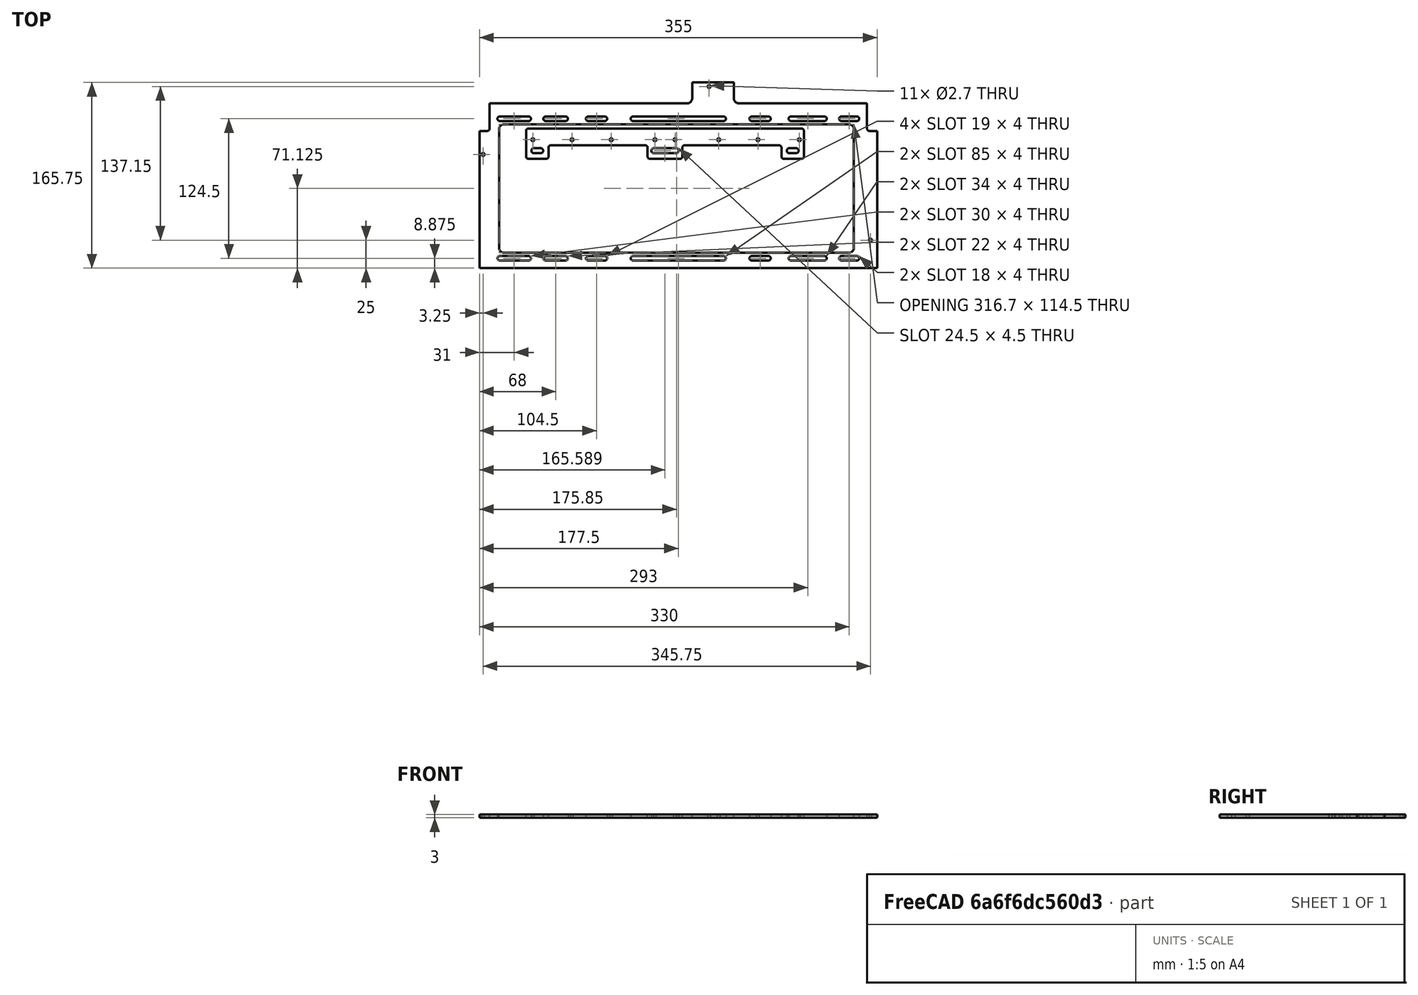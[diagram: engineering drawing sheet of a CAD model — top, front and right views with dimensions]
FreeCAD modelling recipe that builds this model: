
FCSTD DOCUMENT  (FreeCAD 0.19R24291 (Git))
Label: Mesh_Rad_Mount_04
License: All rights reserved
LicenseURL: http://en.wikipedia.org/wiki/All_rights_reserved
objects: Sketcher::SketchObject×2, PartDesign::Pad×2, PartDesign::Body×2, Mesh::Feature×1
note: 8 computed .brp shape members not serialized (recipe doc carries the construction recipe); baked Part::Feature solids carry a one-line shape summary decoded from their .brp

FEATURE [Sketcher::SketchObject] Sketch
  FullyConstrained = true
  MapMode = 5
  Support = -> [XY_Plane]
  expr: Constraints[122] = (142.25mm - 114.5mm) / 2
  expr: Constraints[121] = (124.5mm - 114.5mm) / 2
  sketch-geometry (84):
    g0: LineSegment StartX=190 StartY=152 StartZ=0 EndX=190 EndY=165.75 EndZ=0
    g1: LineSegment StartX=190 StartY=165.75 StartZ=0 EndX=227 EndY=165.75 EndZ=0
    g2: LineSegment StartX=227 StartY=165.75 StartZ=0 EndX=227 EndY=152 EndZ=0
    g3: LineSegment StartX=232 StartY=147 StartZ=0 EndX=346 EndY=147 EndZ=0
    g4: LineSegment StartX=355 StartY=0 StartZ=0 EndX=0 EndY=0 EndZ=0
    g5: LineSegment StartX=7 StartY=122.5 StartZ=0 EndX=0 EndY=122.5 EndZ=0
    g6: LineSegment StartX=0 StartY=0 StartZ=0 EndX=0 EndY=122.5 EndZ=0
    g7: ArcOfCircle CenterX=7 CenterY=124.5 CenterZ=0 NormalX=0 NormalY=0 NormalZ=1 AngleXU=0 Radius=2 StartAngle=4.71239 EndAngle=6.28319
    g8: ArcOfCircle CenterX=18 CenterY=8.875 CenterZ=0 NormalX=0 NormalY=0 NormalZ=1 AngleXU=0 Radius=2 StartAngle=1.5708 EndAngle=4.71239
    g9: ArcOfCircle CenterX=44 CenterY=8.875 CenterZ=0 NormalX=0 NormalY=0 NormalZ=1 AngleXU=0 Radius=2 StartAngle=4.71239 EndAngle=7.85398
    g10: LineSegment StartX=18 StartY=6.875 StartZ=0 EndX=44 EndY=6.875 EndZ=0
    g11: LineSegment StartX=18 StartY=10.875 StartZ=0 EndX=44 EndY=10.875 EndZ=0
    g12: LineSegment StartX=21.7 StartY=128.375 StartZ=0 EndX=330 EndY=128.375 EndZ=0
    g13: LineSegment StartX=334.2 StartY=124.175 StartZ=0 EndX=334.2 EndY=18.075 EndZ=0
    g14: LineSegment StartX=330 StartY=13.875 StartZ=0 EndX=21.7 EndY=13.875 EndZ=0
    g15: LineSegment StartX=17.5 StartY=18.075 StartZ=0 EndX=17.5 EndY=124.175 EndZ=0
    g16: ArcOfCircle CenterX=21.7 CenterY=124.175 CenterZ=0 NormalX=0 NormalY=0 NormalZ=1 AngleXU=0 Radius=4.2 StartAngle=1.5708 EndAngle=3.14159
    g17: ArcOfCircle CenterX=21.7 CenterY=18.075 CenterZ=0 NormalX=0 NormalY=0 NormalZ=1 AngleXU=0 Radius=4.2 StartAngle=3.14159 EndAngle=4.71239
    g18: ArcOfCircle CenterX=330 CenterY=18.075 CenterZ=0 NormalX=0 NormalY=0 NormalZ=1 AngleXU=0 Radius=4.2 StartAngle=4.71239 EndAngle=6.28319
    g19: ArcOfCircle CenterX=330 CenterY=124.175 CenterZ=0 NormalX=0 NormalY=0 NormalZ=1 AngleXU=0 Radius=4.2 StartAngle=1.2e-15 EndAngle=1.5708
    g20: ArcOfCircle CenterX=18 CenterY=133.375 CenterZ=0 NormalX=0 NormalY=0 NormalZ=1 AngleXU=0 Radius=2 StartAngle=1.5708 EndAngle=4.71239
    g21: ArcOfCircle CenterX=44 CenterY=133.375 CenterZ=0 NormalX=0 NormalY=0 NormalZ=1 AngleXU=0 Radius=2 StartAngle=4.71239 EndAngle=7.85398
    g22: LineSegment StartX=18 StartY=131.375 StartZ=0 EndX=44 EndY=131.375 EndZ=0
    g23: LineSegment StartX=18 StartY=135.375 StartZ=0 EndX=44 EndY=135.375 EndZ=0
    g24: ArcOfCircle CenterX=59 CenterY=133.375 CenterZ=0 NormalX=0 NormalY=0 NormalZ=1 AngleXU=0 Radius=2 StartAngle=1.5708 EndAngle=4.71239
    g25: ArcOfCircle CenterX=77 CenterY=133.375 CenterZ=0 NormalX=0 NormalY=0 NormalZ=1 AngleXU=0 Radius=2 StartAngle=4.71239 EndAngle=7.85398
    g26: LineSegment StartX=59 StartY=131.375 StartZ=0 EndX=77 EndY=131.375 EndZ=0
    g27: LineSegment StartX=59 StartY=135.375 StartZ=0 EndX=77 EndY=135.375 EndZ=0
    g28: ArcOfCircle CenterX=278 CenterY=133.375 CenterZ=0 NormalX=0 NormalY=0 NormalZ=1 AngleXU=0 Radius=2 StartAngle=1.5708 EndAngle=4.71239
    g29: ArcOfCircle CenterX=308 CenterY=133.375 CenterZ=0 NormalX=0 NormalY=0 NormalZ=1 AngleXU=0 Radius=2 StartAngle=4.71239 EndAngle=7.85398
    g30: LineSegment StartX=278 StartY=131.375 StartZ=0 EndX=308 EndY=131.375 EndZ=0
    g31: LineSegment StartX=278 StartY=135.375 StartZ=0 EndX=308 EndY=135.375 EndZ=0
    g32: ArcOfCircle CenterX=323 CenterY=133.375 CenterZ=0 NormalX=0 NormalY=0 NormalZ=1 AngleXU=0 Radius=2 StartAngle=1.5708 EndAngle=4.71239
    g33: ArcOfCircle CenterX=337 CenterY=133.375 CenterZ=0 NormalX=0 NormalY=0 NormalZ=1 AngleXU=0 Radius=2 StartAngle=4.71239 EndAngle=7.85398
    g34: LineSegment StartX=323 StartY=131.375 StartZ=0 EndX=337 EndY=131.375 EndZ=0
    g35: LineSegment StartX=323 StartY=135.375 StartZ=0 EndX=337 EndY=135.375 EndZ=0
    g36: ArcOfCircle CenterX=137 CenterY=133.375 CenterZ=0 NormalX=0 NormalY=0 NormalZ=1 AngleXU=0 Radius=2 StartAngle=1.5708 EndAngle=4.71239
    g37: ArcOfCircle CenterX=218 CenterY=133.375 CenterZ=0 NormalX=0 NormalY=0 NormalZ=1 AngleXU=0 Radius=2 StartAngle=4.71239 EndAngle=7.85398
    g38: LineSegment StartX=137 StartY=131.375 StartZ=0 EndX=218 EndY=131.375 EndZ=0
    g39: LineSegment StartX=137 StartY=135.375 StartZ=0 EndX=218 EndY=135.375 EndZ=0
    g40: ArcOfCircle CenterX=59 CenterY=8.875 CenterZ=0 NormalX=0 NormalY=0 NormalZ=1 AngleXU=0 Radius=2 StartAngle=1.5708 EndAngle=4.71239
    g41: ArcOfCircle CenterX=77 CenterY=8.875 CenterZ=0 NormalX=0 NormalY=0 NormalZ=1 AngleXU=0 Radius=2 StartAngle=4.71239 EndAngle=7.85398
    g42: LineSegment StartX=59 StartY=6.875 StartZ=0 EndX=77 EndY=6.875 EndZ=0
    g43: LineSegment StartX=59 StartY=10.875 StartZ=0 EndX=77 EndY=10.875 EndZ=0
    g44: ArcOfCircle CenterX=137 CenterY=8.875 CenterZ=0 NormalX=0 NormalY=0 NormalZ=1 AngleXU=0 Radius=2 StartAngle=1.5708 EndAngle=4.71239
    g45: ArcOfCircle CenterX=218 CenterY=8.875 CenterZ=0 NormalX=0 NormalY=0 NormalZ=1 AngleXU=0 Radius=2 StartAngle=4.71239 EndAngle=7.85398
    g46: LineSegment StartX=137 StartY=6.875 StartZ=0 EndX=218 EndY=6.875 EndZ=0
    g47: LineSegment StartX=137 StartY=10.875 StartZ=0 EndX=218 EndY=10.875 EndZ=0
    g48: ArcOfCircle CenterX=278 CenterY=8.875 CenterZ=0 NormalX=0 NormalY=0 NormalZ=1 AngleXU=0 Radius=2 StartAngle=1.5708 EndAngle=4.71239
    g49: ArcOfCircle CenterX=308 CenterY=8.875 CenterZ=0 NormalX=0 NormalY=0 NormalZ=1 AngleXU=0 Radius=2 StartAngle=4.71239 EndAngle=7.85398
    g50: LineSegment StartX=278 StartY=6.875 StartZ=0 EndX=308 EndY=6.875 EndZ=0
    g51: LineSegment StartX=278 StartY=10.875 StartZ=0 EndX=308 EndY=10.875 EndZ=0
    g52: ArcOfCircle CenterX=323 CenterY=8.875 CenterZ=0 NormalX=0 NormalY=0 NormalZ=1 AngleXU=0 Radius=2 StartAngle=1.5708 EndAngle=4.71239
    g53: ArcOfCircle CenterX=337 CenterY=8.875 CenterZ=0 NormalX=0 NormalY=0 NormalZ=1 AngleXU=0 Radius=2 StartAngle=4.71239 EndAngle=7.85398
    g54: LineSegment StartX=323 StartY=6.875 StartZ=0 EndX=337 EndY=6.875 EndZ=0
    g55: LineSegment StartX=323 StartY=10.875 StartZ=0 EndX=337 EndY=10.875 EndZ=0
    g56: Circle CenterX=3.25 CenterY=101.5 CenterZ=0 NormalX=0 NormalY=0 NormalZ=1 AngleXU=0 Radius=1.35
    g57: Circle CenterX=205 CenterY=162.15 CenterZ=0 NormalX=0 NormalY=0 NormalZ=1 AngleXU=0 Radius=1.35
    g58: Circle CenterX=349 CenterY=25 CenterZ=0 NormalX=0 NormalY=0 NormalZ=1 AngleXU=0 Radius=1.35
    g59: LineSegment StartX=346 StartY=147 StartZ=0 EndX=346 EndY=124.5 EndZ=0
    g60: LineSegment StartX=348 StartY=122.5 StartZ=0 EndX=355 EndY=122.5 EndZ=0
    g61: LineSegment StartX=355 StartY=0 StartZ=0 EndX=355 EndY=122.5 EndZ=0
    g62: ArcOfCircle CenterX=348 CenterY=124.5 CenterZ=0 NormalX=0 NormalY=0 NormalZ=1 AngleXU=0 Radius=2 StartAngle=3.14159 EndAngle=4.71239
    g63: ArcOfCircle CenterX=232 CenterY=152 CenterZ=0 NormalX=0 NormalY=0 NormalZ=1 AngleXU=0 Radius=5 StartAngle=3.14159 EndAngle=4.71239
    g64: ArcOfCircle CenterX=185 CenterY=152 CenterZ=0 NormalX=0 NormalY=0 NormalZ=1 AngleXU=0 Radius=5 StartAngle=4.71239 EndAngle=6.28319
    g65: ArcOfCircle CenterX=97 CenterY=133.375 CenterZ=0 NormalX=0 NormalY=0 NormalZ=1 AngleXU=0 Radius=2 StartAngle=1.5708 EndAngle=4.71239
    g66: ArcOfCircle CenterX=112 CenterY=133.375 CenterZ=0 NormalX=0 NormalY=0 NormalZ=1 AngleXU=0 Radius=2 StartAngle=4.71239 EndAngle=7.85398
    g67: LineSegment StartX=97 StartY=131.375 StartZ=0 EndX=112 EndY=131.375 EndZ=0
    g68: LineSegment StartX=97 StartY=135.375 StartZ=0 EndX=112 EndY=135.375 EndZ=0
    g69: ArcOfCircle CenterX=97 CenterY=8.875 CenterZ=0 NormalX=0 NormalY=0 NormalZ=1 AngleXU=0 Radius=2 StartAngle=1.5708 EndAngle=4.71239
    g70: ArcOfCircle CenterX=112 CenterY=8.875 CenterZ=0 NormalX=0 NormalY=0 NormalZ=1 AngleXU=0 Radius=2 StartAngle=4.71239 EndAngle=7.85398
    g71: LineSegment StartX=97 StartY=6.875 StartZ=0 EndX=112 EndY=6.875 EndZ=0
    g72: LineSegment StartX=97 StartY=10.875 StartZ=0 EndX=112 EndY=10.875 EndZ=0
    g73: ArcOfCircle CenterX=243 CenterY=8.875 CenterZ=0 NormalX=0 NormalY=0 NormalZ=1 AngleXU=0 Radius=2 StartAngle=1.5708 EndAngle=4.71239
    g74: ArcOfCircle CenterX=258 CenterY=8.875 CenterZ=0 NormalX=0 NormalY=0 NormalZ=1 AngleXU=0 Radius=2 StartAngle=4.71239 EndAngle=7.85398
    g75: LineSegment StartX=243 StartY=6.875 StartZ=0 EndX=258 EndY=6.875 EndZ=0
    g76: LineSegment StartX=243 StartY=10.875 StartZ=0 EndX=258 EndY=10.875 EndZ=0
    g77: ArcOfCircle CenterX=243 CenterY=133.375 CenterZ=0 NormalX=0 NormalY=0 NormalZ=1 AngleXU=0 Radius=2 StartAngle=1.5708 EndAngle=4.71239
    g78: ArcOfCircle CenterX=258 CenterY=133.375 CenterZ=0 NormalX=0 NormalY=0 NormalZ=1 AngleXU=0 Radius=2 StartAngle=4.71239 EndAngle=7.85398
    g79: LineSegment StartX=243 StartY=131.375 StartZ=0 EndX=258 EndY=131.375 EndZ=0
    g80: LineSegment StartX=243 StartY=135.375 StartZ=0 EndX=258 EndY=135.375 EndZ=0
    g81: LineSegment StartX=185 StartY=147 StartZ=0 EndX=9 EndY=147 EndZ=0
    g82: LineSegment StartX=9 StartY=128 StartZ=0 EndX=9 EndY=147 EndZ=0
    g83: LineSegment StartX=9 StartY=124.5 StartZ=0 EndX=9 EndY=128 EndZ=0
  constraints (217):
    c: Coincident(g0,g1)
    c: Horizontal(g1)
    c: Coincident(g1,g2)
    c: Horizontal(g3)
    c: Horizontal(g4)
    c: Vertical(g2)
    c: Vertical(g0)
    c: Horizontal(g5)
    c: DistanceY(g4,g3) = 147
    c: Coincident(g6,g4)
    c: Coincident(g6,g5)
    c: Tangent(g5,g7) = 1.5708
    c: DistanceX(g4,g4) = 355
    c: Coincident(g4,g-1)
    c: Tangent(g8,g11) = 1.5708
    c: Tangent(g8,g10) = -1.5708
    c: Tangent(g10,g9) = -1.5708
    c: Tangent(g11,g9) = 1.5708
    c: Horizontal(g10)
    c: Equal(g8,g9)
    c: Horizontal(g12)
    c: Horizontal(g14)
    c: Vertical(g13)
    c: Vertical(g15)
    c: Tangent(g12,g16) = 1.5708
    c: Tangent(g15,g16) = 1.5708
    c: Tangent(g15,g17) = 1.5708
    c: Tangent(g14,g17) = 1.5708
    c: Tangent(g14,g18) = 1.5708
    c: Tangent(g13,g18) = 1.5708
    c: Tangent(g12,g19) = 1.5708
    c: Tangent(g13,g19) = 1.5708
    c: Radius(g16) = 4.2
    c: Equal(g16,g17)
    c: Equal(g16,g19)
    c: Equal(g16,g18)
    c: DistanceX(g4,g15) = 17.5
    c: Tangent(g20,g23) = 1.5708
    c: Tangent(g20,g22) = -1.5708
    c: Tangent(g22,g21) = -1.5708
    c: Tangent(g23,g21) = 1.5708
    c: Horizontal(g22)
    c: Equal(g20,g21)
    c: Tangent(g24,g27) = 1.5708
    c: Tangent(g24,g26) = -1.5708
    c: Tangent(g26,g25) = -1.5708
    c: Tangent(g27,g25) = 1.5708
    c: Horizontal(g26)
    c: Equal(g24,g25)
    c: Tangent(g28,g31) = 1.5708
    c: Tangent(g28,g30) = -1.5708
    c: Tangent(g30,g29) = -1.5708
    c: Tangent(g31,g29) = 1.5708
    c: Horizontal(g30)
    c: Equal(g28,g29)
    c: Tangent(g32,g35) = 1.5708
    c: Tangent(g32,g34) = -1.5708
    c: Tangent(g34,g33) = -1.5708
    c: Tangent(g35,g33) = 1.5708
    c: Horizontal(g34)
    c: Equal(g32,g33)
    c: Tangent(g36,g39) = 1.5708
    c: Tangent(g36,g38) = -1.5708
    c: Tangent(g38,g37) = -1.5708
    c: Tangent(g39,g37) = 1.5708
    c: Horizontal(g38)
    c: Equal(g36,g37)
    c: Tangent(g40,g43) = 1.5708
    c: Tangent(g40,g42) = -1.5708
    c: Tangent(g42,g41) = -1.5708
    c: Tangent(g43,g41) = 1.5708
    c: Horizontal(g42)
    c: Equal(g40,g41)
    c: Tangent(g44,g47) = 1.5708
    c: Tangent(g44,g46) = -1.5708
    c: Tangent(g46,g45) = -1.5708
    c: Tangent(g47,g45) = 1.5708
    c: Horizontal(g46)
    c: Equal(g44,g45)
    c: Tangent(g48,g51) = 1.5708
    c: Tangent(g48,g50) = -1.5708
    c: Tangent(g50,g49) = -1.5708
    c: Tangent(g51,g49) = 1.5708
    c: Horizontal(g50)
    c: Equal(g48,g49)
    c: Tangent(g52,g55) = 1.5708
    c: Tangent(g52,g54) = -1.5708
    c: Tangent(g54,g53) = -1.5708
    c: Tangent(g55,g53) = 1.5708
    c: Horizontal(g54)
    c: Equal(g52,g53)
    c: Radius(g52) = 2
    c: Equal(g52,g48)
    c: Equal(g52,g44)
    c: Equal(g52,g40)
    c: Equal(g52,g8)
    c: Equal(g52,g20)
    c: Equal(g52,g24)
    c: Equal(g52,g36)
    c: Equal(g52,g28)
    c: Equal(g52,g32)
    c: Horizontal(g53,g49)
    c: Horizontal(g49,g45)
    c: Horizontal(g45,g41)
    c: Horizontal(g41,g9)
    c: Horizontal(g33,g29)
    c: Horizontal(g29,g25)
    c: Horizontal(g25,g21)
    c: Horizontal(g21,g37)
    c: Vertical(g20,g8)
    c: Vertical(g21,g9)
    c: Vertical(g24,g40)
    c: Vertical(g25,g41)
    c: Vertical(g36,g44)
    c: Vertical(g45,g37)
    c: Vertical(g48,g28)
    c: Vertical(g49,g29)
    c: Vertical(g52,g32)
    c: Vertical(g33,g53)
    c: DistanceY(g8,g20) = 124.5
    c: DistanceY(g14,g12) = 114.5
    c: DistanceY(g8,g14) = 5
    c: DistanceY(g4,g14) = 13.875
    c: DistanceX(g24,g25) = 18
    c: DistanceX(g20,g21) = 26
    c: DistanceX(g21,g24) = 15
    c: DistanceX(g4,g20) = 18
    c: DistanceX(g4,g56) = 3.25
    c: DistanceY(g3,g57) = 15.15
    c: DistanceY(g4,g58) = 25
    c: DistanceX(g58,g4) = 6
    c: Vertical(g59)
    c: Horizontal(g60)
    c: Coincident(g61,g4)
    c: Coincident(g61,g60)
    c: Vertical(g61)
    c: Horizontal(g5,g60)
    c: Tangent(g59,g62) = -1.5708
    c: Tangent(g60,g62) = -1.5708
    c: Radius(g62) = 2
    c: Tangent(g2,g63) = -1.5708
    c: Tangent(g3,g63) = -1.5708
    c: DistanceY(g3,g1) = 18.75
    c: Tangent(g0,g64) = -1.5708
    c: DistanceX(g0,g1) = 37
    c: Radius(g64) = 5
    c: Equal(g64,g63)
    c: DistanceX(g32,g33) = 14
    c: DistanceX(g29,g32) = 15
    c: DistanceX(g28,g29) = 30
    c: DistanceX(g25,g36) = 60
    c: DistanceX(g37,g28) = 60
    c: Diameter(g56) = 2.7
    c: Equal(g56,g57)
    c: Equal(g56,g58)
    c: Tangent(g65,g68) = 1.5708
    c: Tangent(g65,g67) = -1.5708
    c: Tangent(g67,g66) = -1.5708
    c: Tangent(g68,g66) = 1.5708
    c: Horizontal(g67)
    c: Equal(g65,g66)
    c: Tangent(g69,g72) = 1.5708
    c: Tangent(g69,g71) = -1.5708
    c: Tangent(g71,g70) = -1.5708
    c: Tangent(g72,g70) = 1.5708
    c: Horizontal(g71)
    c: Equal(g69,g70)
    c: Tangent(g73,g76) = 1.5708
    c: Tangent(g73,g75) = -1.5708
    c: Tangent(g75,g74) = -1.5708
    c: Tangent(g76,g74) = 1.5708
    c: Horizontal(g75)
    c: Equal(g73,g74)
    c: Tangent(g77,g80) = 1.5708
    c: Tangent(g77,g79) = -1.5708
    c: Tangent(g79,g78) = -1.5708
    c: Tangent(g80,g78) = 1.5708
    c: Horizontal(g79)
    c: Equal(g77,g78)
    c: DistanceX(g25,g65) = 20
    c: DistanceX(g66,g36) = 25
    c: DistanceX(g78,g28) = 20
    c: DistanceX(g37,g77) = 25
    c: Horizontal(g77,g66)
    c: Horizontal(g66,g36)
    c: Diameter(g65) = 4
    c: Equal(g65,g77)
    c: Equal(g65,g73)
    c: Equal(g65,g70)
    c: Horizontal(g70,g44)
    c: Horizontal(g44,g73)
    c: Vertical(g65,g69)
    c: Vertical(g70,g66)
    c: Vertical(g73,g77)
    c: Vertical(g74,g78)
    c: DistanceY(g5,g82) = 5.5
    c: Coincident(g81,g64)
    c: Horizontal(g81)
    c: DistanceY(g82,g81) = 19
    c: DistanceY(g56,g81) = 45.5
    c: Coincident(g82,g81)
    c: Vertical(g82)
    c: Radius(g7) = 2
    c: Coincident(g83,g7)
    c: Coincident(g83,g82)
    c: Vertical(g83)
    c: Vertical(g5,g4)
    c: Horizontal(g64,g3)
    c: DistanceX(g5,g5) = 7
    c: DistanceX(g33,g60) = 18
    c: DistanceX(g57,g60) = 150
    c: DistanceX(g1,g60) = 128
    c: DistanceX(g60,g60) = 7
    c: Coincident(g3,g59)
    c: DistanceX(g19,g33) = 7
    c: Horizontal(g7,g7)
    c: Vertical(g64,g64)
FEATURE [Mesh::Feature] TOP_02__1_  label="TOP_02 (1)"
  Placement = pos=(320,-224.75,0) rot=(0,0,1;0rad)
FEATURE [Sketcher::SketchObject] Sketch001
  FullyConstrained = false
  MapMode = 5
  Support = -> [XY_Plane001]
  expr: Constraints[80] = (31mm - 20mm) / 2
  expr: Constraints[56] = (248mm - 31mm) / 2
  sketch-geometry (44):
    g0: LineSegment StartX=59.5885 StartY=97.6384 StartZ=0 EndX=43.5885 EndY=97.6384 EndZ=0
    g1: LineSegment StartX=41.5885 StartY=99.6384 StartZ=0 EndX=41.5885 EndY=122.638 EndZ=0
    g2: LineSegment StartX=43.5885 StartY=124.638 StartZ=0 EndX=287.588 EndY=124.638 EndZ=0
    g3: LineSegment StartX=289.588 StartY=122.638 StartZ=0 EndX=289.588 EndY=99.6384 EndZ=0
    g4: LineSegment StartX=287.588 StartY=97.6384 StartZ=0 EndX=271.588 EndY=97.6384 EndZ=0
    g5: LineSegment StartX=269.588 StartY=99.6384 StartZ=0 EndX=269.588 EndY=107.638 EndZ=0
    g6: LineSegment StartX=267.588 StartY=109.638 StartZ=0 EndX=183.088 EndY=109.638 EndZ=0
    g7: LineSegment StartX=181.088 StartY=107.638 StartZ=0 EndX=181.088 EndY=99.6384 EndZ=0
    g8: LineSegment StartX=179.088 StartY=97.6384 StartZ=0 EndX=152.088 EndY=97.6384 EndZ=0
    g9: LineSegment StartX=150.088 StartY=99.6384 StartZ=0 EndX=150.088 EndY=107.638 EndZ=0
    g10: LineSegment StartX=148.088 StartY=109.638 StartZ=0 EndX=63.5885 EndY=109.638 EndZ=0
    g11: LineSegment StartX=61.5885 StartY=107.638 StartZ=0 EndX=61.5885 EndY=99.6384 EndZ=0
    g12: ArcOfCircle CenterX=267.588 CenterY=107.638 CenterZ=0 NormalX=0 NormalY=0 NormalZ=1 AngleXU=0 Radius=2 StartAngle=2.1e-15 EndAngle=1.5708
    g13: ArcOfCircle CenterX=63.5885 CenterY=107.638 CenterZ=0 NormalX=0 NormalY=0 NormalZ=1 AngleXU=0 Radius=2 StartAngle=1.5708 EndAngle=3.14159
    g14: ArcOfCircle CenterX=148.088 CenterY=107.638 CenterZ=0 NormalX=0 NormalY=0 NormalZ=1 AngleXU=0 Radius=2 StartAngle=3e-16 EndAngle=1.5708
    g15: ArcOfCircle CenterX=152.088 CenterY=99.6384 CenterZ=0 NormalX=0 NormalY=0 NormalZ=1 AngleXU=0 Radius=2 StartAngle=3.14159 EndAngle=4.71239
    g16: ArcOfCircle CenterX=179.088 CenterY=99.6384 CenterZ=0 NormalX=0 NormalY=0 NormalZ=1 AngleXU=0 Radius=2 StartAngle=4.71239 EndAngle=6.28319
    g17: ArcOfCircle CenterX=271.588 CenterY=99.6384 CenterZ=0 NormalX=0 NormalY=0 NormalZ=1 AngleXU=0 Radius=2 StartAngle=3.14159 EndAngle=4.71239
    g18: ArcOfCircle CenterX=59.5885 CenterY=99.6384 CenterZ=0 NormalX=0 NormalY=0 NormalZ=1 AngleXU=0 Radius=2 StartAngle=4.71239 EndAngle=6.28319
    g19: ArcOfCircle CenterX=43.5885 CenterY=99.6384 CenterZ=0 NormalX=0 NormalY=0 NormalZ=1 AngleXU=0 Radius=2 StartAngle=3.14159 EndAngle=4.71239
    g20: ArcOfCircle CenterX=287.588 CenterY=99.6384 CenterZ=0 NormalX=0 NormalY=0 NormalZ=1 AngleXU=0 Radius=2 StartAngle=4.71239 EndAngle=6.28319
    g21: ArcOfCircle CenterX=43.5885 CenterY=122.638 CenterZ=0 NormalX=0 NormalY=0 NormalZ=1 AngleXU=0 Radius=2 StartAngle=1.5708 EndAngle=3.14159
    g22: ArcOfCircle CenterX=287.588 CenterY=122.638 CenterZ=0 NormalX=0 NormalY=0 NormalZ=1 AngleXU=0 Radius=2 StartAngle=-9e-16 EndAngle=1.5708
    g23: ArcOfCircle CenterX=183.088 CenterY=107.638 CenterZ=0 NormalX=0 NormalY=0 NormalZ=1 AngleXU=0 Radius=2 StartAngle=1.5708 EndAngle=3.14159
    g24: ArcOfCircle CenterX=155.588 CenterY=104.888 CenterZ=0 NormalX=0 NormalY=0 NormalZ=1 AngleXU=0 Radius=2.25 StartAngle=1.5708 EndAngle=4.71239
    g25: ArcOfCircle CenterX=175.588 CenterY=104.888 CenterZ=0 NormalX=0 NormalY=0 NormalZ=1 AngleXU=0 Radius=2.25 StartAngle=4.71239 EndAngle=7.85398
    g26: LineSegment StartX=155.588 StartY=102.638 StartZ=0 EndX=175.588 EndY=102.638 EndZ=0
    g27: LineSegment StartX=155.588 StartY=107.138 StartZ=0 EndX=175.588 EndY=107.138 EndZ=0
    g28: ArcOfCircle CenterX=48.5885 CenterY=104.888 CenterZ=0 NormalX=0 NormalY=0 NormalZ=1 AngleXU=0 Radius=2.25 StartAngle=1.5708 EndAngle=4.71239
    g29: ArcOfCircle CenterX=54.5885 CenterY=104.888 CenterZ=0 NormalX=0 NormalY=0 NormalZ=1 AngleXU=0 Radius=2.25 StartAngle=4.71239 EndAngle=7.85398
    g30: LineSegment StartX=48.5885 StartY=102.638 StartZ=0 EndX=54.5885 EndY=102.638 EndZ=0
    g31: LineSegment StartX=48.5885 StartY=107.138 StartZ=0 EndX=54.5885 EndY=107.138 EndZ=0
    g32: ArcOfCircle CenterX=276.588 CenterY=104.888 CenterZ=0 NormalX=0 NormalY=0 NormalZ=1 AngleXU=0 Radius=2.25 StartAngle=1.5708 EndAngle=4.71239
    g33: ArcOfCircle CenterX=282.588 CenterY=104.888 CenterZ=0 NormalX=0 NormalY=0 NormalZ=1 AngleXU=0 Radius=2.25 StartAngle=4.71239 EndAngle=7.85398
    g34: LineSegment StartX=276.588 StartY=102.638 StartZ=0 EndX=282.588 EndY=102.638 EndZ=0
    g35: LineSegment StartX=276.588 StartY=107.138 StartZ=0 EndX=282.588 EndY=107.138 EndZ=0
    g36: Circle CenterX=47.5885 CenterY=114.638 CenterZ=0 NormalX=0 NormalY=0 NormalZ=1 AngleXU=0 Radius=1.35
    g37: Circle CenterX=117.588 CenterY=114.638 CenterZ=0 NormalX=0 NormalY=0 NormalZ=1 AngleXU=0 Radius=1.35
    g38: Circle CenterX=82.5885 CenterY=114.638 CenterZ=0 NormalX=0 NormalY=0 NormalZ=1 AngleXU=0 Radius=1.35
    g39: Circle CenterX=156.588 CenterY=114.638 CenterZ=0 NormalX=0 NormalY=0 NormalZ=1 AngleXU=0 Radius=1.35
    g40: Circle CenterX=174.588 CenterY=114.638 CenterZ=0 NormalX=0 NormalY=0 NormalZ=1 AngleXU=0 Radius=1.35
    g41: Circle CenterX=248.588 CenterY=114.638 CenterZ=0 NormalX=0 NormalY=0 NormalZ=1 AngleXU=0 Radius=1.35
    g42: Circle CenterX=285.588 CenterY=114.638 CenterZ=0 NormalX=0 NormalY=0 NormalZ=1 AngleXU=0 Radius=1.35
    g43: Circle CenterX=213.588 CenterY=114.638 CenterZ=0 NormalX=0 NormalY=0 NormalZ=1 AngleXU=0 Radius=1.35
  constraints (112):
    c: Horizontal(g2)
    c: Vertical(g3)
    c: Vertical(g5)
    c: Vertical(g9)
    c: Vertical(g1)
    c: Vertical(g11)
    c: Vertical(g7)
    c: Horizontal(g0)
    c: Horizontal(g8)
    c: Horizontal(g4)
    c: Horizontal(g10)
    c: Horizontal(g6)
    c: Tangent(g6,g12) = -1.5708
    c: Tangent(g5,g12) = -1.5708
    c: Tangent(g11,g13) = -1.5708
    c: Tangent(g10,g13) = -1.5708
    c: Tangent(g10,g14) = -1.5708
    c: Tangent(g9,g14) = -1.5708
    c: Tangent(g9,g15) = 1.5708
    c: Tangent(g8,g15) = 1.5708
    c: Tangent(g8,g16) = 1.5708
    c: Tangent(g7,g16) = 1.5708
    c: Tangent(g5,g17) = 1.5708
    c: Tangent(g4,g17) = 1.5708
    c: Tangent(g11,g18) = 1.5708
    c: Tangent(g0,g18) = 1.5708
    c: Tangent(g1,g19) = 1.5708
    c: Tangent(g0,g19) = 1.5708
    c: Tangent(g3,g20) = 1.5708
    c: Tangent(g4,g20) = 1.5708
    c: DistanceX(g5,g3) = 20
    c: DistanceX(g1,g11) = 20
    c: Tangent(g1,g21) = 1.5708
    c: Tangent(g2,g21) = 1.5708
    c: Tangent(g2,g22) = 1.5708
    c: Tangent(g3,g22) = 1.5708
    c: DistanceX(g1,g3) = 248
    c: DistanceY(g4,g2) = 27
    c: Radius(g22) = 2
    c: Equal(g22,g20)
    c: Equal(g22,g21)
    c: Equal(g22,g19)
    c: Horizontal(g4,g8)
    c: Horizontal(g8,g0)
    c: Tangent(g7,g23) = -1.5708
    c: Tangent(g6,g23) = -1.5708
    c: Horizontal(g10,g6)
    c: Radius(g13) = 2
    c: Equal(g13,g14)
    c: Equal(g13,g23)
    c: Equal(g13,g12)
    c: Radius(g16) = 2
    c: Equal(g16,g15)
    c: Radius(g17) = 2
    c: Equal(g17,g18)
    c: DistanceX(g9,g7) = 31
    c: DistanceX(g1,g9) = 108.5
    c: DistanceY(g4,g6) = 12
    c: Tangent(g24,g27) = 1.5708
    c: Tangent(g24,g26) = -1.5708
    c: Tangent(g26,g25) = -1.5708
    c: Tangent(g27,g25) = 1.5708
    c: Horizontal(g26)
    c: Equal(g24,g25)
    c: Tangent(g28,g31) = 1.5708
    c: Tangent(g28,g30) = -1.5708
    c: Tangent(g30,g29) = -1.5708
    c: Tangent(g31,g29) = 1.5708
    c: Horizontal(g30)
    c: Equal(g28,g29)
    c: Tangent(g32,g35) = 1.5708
    c: Tangent(g32,g34) = -1.5708
    c: Tangent(g34,g33) = -1.5708
    c: Tangent(g35,g33) = 1.5708
    c: Horizontal(g34)
    c: Equal(g32,g33)
    c: Diameter(g29) = 4.5
    c: Equal(g29,g24)
    c: Equal(g29,g32)
    c: DistanceX(g24,g25) = 20
    c: DistanceX(g9,g24) = 5.5
    c: DistanceX(g29,g24) = 101
    c: DistanceX(g28,g29) = 6
    c: DistanceX(g25,g32) = 101
    c: DistanceX(g32,g33) = 6
    c: DistanceY(g8,g24) = 5
    c: Horizontal(g28,g24)
    c: Horizontal(g24,g32)
    c: Diameter(g42) = 2.7
    c: Equal(g42,g43)
    c: Equal(g42,g41)
    c: Equal(g42,g40)
    c: Equal(g42,g39)
    c: Equal(g42,g38)
    c: Equal(g42,g37)
    c: Equal(g42,g36)
    c: Horizontal(g36,g37)
    c: Horizontal(g37,g38)
    c: Horizontal(g38,g39)
    c: Horizontal(g39,g40)
    c: Horizontal(g40,g41)
    c: Horizontal(g41,g43)
    c: Horizontal(g43,g42)
    c: DistanceX(g21,g36) = 4
    c: DistanceX(g42,g3) = 4
    c: DistanceX(g39,g40) = 18
    c: DistanceX(g40,g41) = 74
    c: DistanceX(g38,g39) = 74
    c: DistanceX(g36,g38) = 35
    c: DistanceX(g38,g37) = 35
    c: DistanceX(g43,g41) = 35
    c: DistanceY(g28,g36) = 9.75
FEATURE [PartDesign::Pad] Pad
  Direction = (1,1,1)
  Length = 3
  Length2 = 100
  Profile = -> Sketch
  Type = 0
FEATURE [PartDesign::Body] Body
  Group = -> [Sketch,Pad]
  Origin = -> Origin
  Tip = -> Pad
FEATURE [PartDesign::Pad] Pad001
  Direction = (1,1,1)
  Length = 3
  Length2 = 100
  Profile = -> Sketch001
  Type = 0
FEATURE [PartDesign::Body] Body001
  Group = -> [Sketch001,Pad001]
  Origin = -> Origin001
  Tip = -> Pad001
